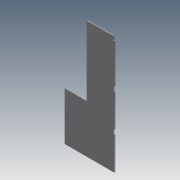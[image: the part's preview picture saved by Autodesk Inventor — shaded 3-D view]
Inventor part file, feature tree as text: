
AUTODESK INVENTOR PART (.ipt)
format: ipt  version: 2011 (Build 150239000, 239)  size: 864,768 bytes
history: native  units: in
note: dims shown in document units (in); Inventor stores cm internally (conversion verified against a paired STEP export)
features: sketch x39, extrude x38
ambient origin geometry x8: Origin, YZ Plane, XZ Plane, XY Plane, X Axis, Y Axis, Z Axis, Center Point
bodies: Solid1 (feature_tree)
feature tree (77):
  extrude  "Extrusion1"  Depth=35.0in
  extrude  "Extrusion2"  Depth=0.25in
  extrude  "Extrusion3"  Depth=2.0in
  extrude  "Extrusion4"  Depth=2.0in
  extrude  "Extrusion5"  Depth=2.0in
  extrude  "Extrusion6"  Depth=2.0in
  extrude  "Extrusion7"  Depth=2.0in
  extrude  "Extrusion8"  Depth=2.0in
  extrude  "Extrusion9"  Depth=2.0in
  extrude  "Extrusion10"  Depth=2.0in
  extrude  "Extrusion11"  Depth=0.25in TaperAngle=0.0deg
  sketch  "Sketch12"  dims[d24=0.25in d25=0.25in d26=0.0in]
  extrude  "Extrusion12"  Depth=0.25in TaperAngle=0.0deg
  extrude  "Extrusion13"  Depth=0.25in
  extrude  "Extrusion14"  Depth=2.0in
  extrude  "Extrusion15"  Depth=1.0in
  extrude  "Extrusion16"  Depth=2.0in
  extrude  "Extrusion17"  Depth=1.0in TaperAngle=0.0deg
  extrude  "Extrusion18"  Depth=1.0in TaperAngle=0.0deg
  extrude  "Extrusion19"  Depth=1.0in TaperAngle=0.0deg
  extrude  "Extrusion20"  Depth=1.75in
  extrude  "Extrusion21"  Depth=1.75in
  extrude  "Extrusion22"  Depth=0.156in
  extrude  "Extrusion23"  Depth=0.25in TaperAngle=0.0deg
  extrude  "Extrusion24"  Depth=0.25in
  extrude  "Extrusion25"  Depth=0.25in
  extrude  "Extrusion26"  Depth=0.156in
  extrude  "Extrusion27"  Depth=0.25in
  extrude  "Extrusion28"  Depth=10.35in
  extrude  "Extrusion29"  Depth=1.0in TaperAngle=0.0deg
  extrude  "Extrusion30"  Depth=1.0in TaperAngle=0.0deg
  extrude  "Extrusion31"  Depth=1.0in TaperAngle=0.0deg
  extrude  "Extrusion32"  Depth=0.25in TaperAngle=0.0deg
  extrude  "Extrusion33"  Depth=5.75in
  extrude  "Extrusion34"  Depth=31.14in
  extrude  "Extrusion35"  Depth=1.0in TaperAngle=0.0deg
  extrude  "Extrusion36"  Depth=0.25in
  extrude  "Extrusion37"  Depth=0.25in
  extrude  "Extrusion38"  Depth=0.25in TaperAngle=0.0deg
  sketch  "Sketch1"  dims[d0=12.85in d1=35.0in]
  sketch  "Sketch2"  dims[d2=0.25in d3=0.0in d4=0.25in]
  sketch  "Sketch3"  dims[d5=2.0in d6=2.0in]
  sketch  "Sketch4"  dims[d7=2.0in d8=2.0in]
  sketch  "Sketch5"  dims[d9=2.0in d10=2.0in]
  sketch  "Sketch6"  dims[d11=2.0in d12=2.0in]
  sketch  "Sketch7"  dims[d13=2.0in d14=2.0in]
  sketch  "Sketch8"  dims[d15=2.0in d16=2.0in]
  sketch  "Sketch9"  dims[d17=2.0in d18=2.0in]
  sketch  "Sketch10"  dims[d19=2.0in d20=2.0in]
  sketch  "Sketch11"  dims[d21=2.0in d22=0.25in d23=0.0in]
  sketch  "Sketch13"  dims[d27=6.175in d28=0.25in]
  sketch  "Sketch14"  dims[d29=1.0in d30=2.0in]
  sketch  "Sketch15"  dims[d31=2.0in d32=1.0in]
  sketch  "Sketch16"  dims[d33=2.0in d34=2.0in]
  sketch  "Sketch17"  dims[d35=0.25in d36=0.0in d37=1.0in d38=0.0in]
  sketch  "Sketch18"  dims[d39=1.0in d40=0.0in d41=1.0in d42=0.0in]
  sketch  "Sketch19"  dims[d43=0.25in d44=1.0in d45=0.0in]
  sketch  "Sketch20"  dims[d46=0.5in d47=1.75in]
  sketch  "Sketch21"  dims[d48=0.5in d49=1.75in]
  sketch  "Sketch22"  dims[d50=0.156in d51=0.156in]
  sketch  "Sketch23"  dims[d52=1.0in d53=0.0in d54=0.25in d55=0.0in]
  sketch  "Sketch24"  dims[d56=0.25in d57=0.0in d58=0.25in]
  sketch  "Sketch25"  dims[d59=1.75in d60=0.25in]
  sketch  "Sketch26"  dims[d61=0.156in d62=0.156in]
  sketch  "Sketch27"  dims[d63=0.25in d64=0.0in d65=0.25in]
  sketch  "Sketch28"  dims[d66=1.0in d67=10.35in]
  sketch  "Sketch29"  dims[d68=0.25in d69=1.0in d70=0.0in]
  sketch  "Sketch30"  dims[d71=0.25in d72=0.0in d73=1.0in d74=0.0in]
  sketch  "Sketch31"  dims[d75=1.0in d76=0.0in d77=1.0in d78=0.0in]
  sketch  "Sketch32"  dims[d79=0.25in d80=0.0in d81=0.25in d82=0.0in]
  sketch  "Sketch33"  dims[d83=12.25in d84=5.75in]
  sketch  "Sketch34"  dims[d85=1.0in d86=0.0in d87=31.14in]
  sketch  "Sketch35"  dims[d88=0.25in d89=1.0in d90=0.0in]
  sketch  "Sketch36"  dims[d91=1.0in d92=0.0in d93=0.25in]
  sketch  "Sketch37"  dims[d94=1.0in d95=0.0in d96=0.25in]
  sketch  "Sketch38"  dims[d97=0.24in d98=0.25in d99=0.0in]
  sketch  "Sketch39"  dims[d100=0.25in d101=0.25in d102=0.0in d103=0.25in d104=0.25in d105=0.0in d106=0.25in d107=0.25in d108=0.0in d109=0.25in d110=1.0in d111=0.0in d112=3.25in d113=0.25in d114=1.0in d115=0.0in d116=0.75in d117=1.0in d118=0.0in d119=9.5in d120=0.25in d121=0.5in d122=0.25in d123=1.0in d124=0.0in d125=0.5in d126=1.0in d127=0.0in d128=8.25in d129=1.0in d130=0.25in d131=1.0in d132=0.0in d133=0.25in d134=1.0in d135=1.0in d136=0.0in d137=0.25in d138=0.0in d139=4.912in d140=5.603in d141=0.185in d142=0.25in d143=0.0in d144=5.418in d145=8.593in d146=0.185in d147=0.185in d148=0.25in d149=0.0in d150=0.5in d151=0.5in d152=1.0in d153=0.0in]
